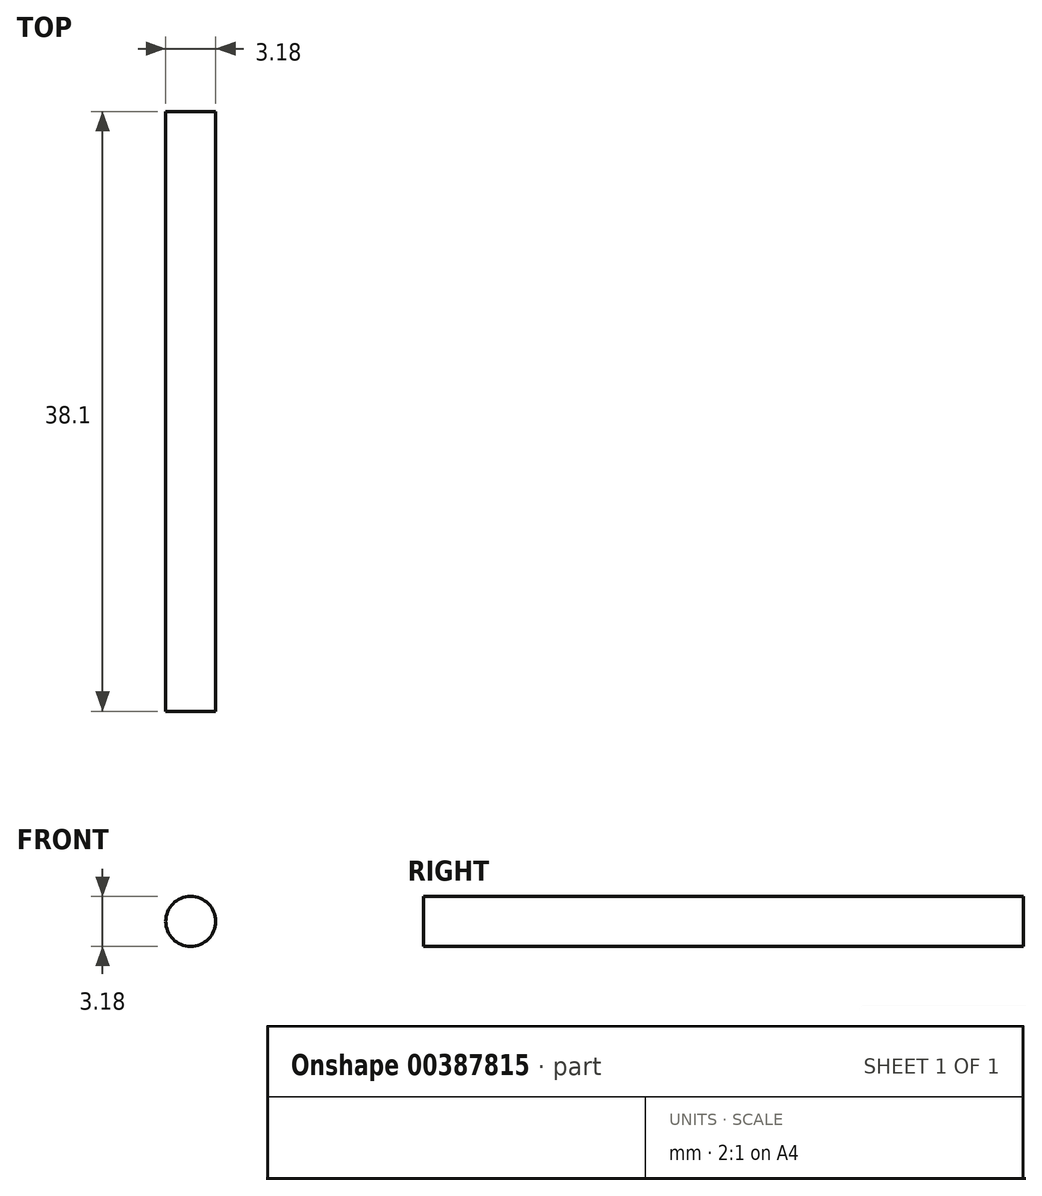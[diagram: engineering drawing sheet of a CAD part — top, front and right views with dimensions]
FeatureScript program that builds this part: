
annotation { "Feature Type Name" : "Feature", "Feature Type Description" : "" }
export const myFeature = defineFeature(function(context is Context, id is Id, definition is map)
    precondition{}
    {
        {
            var Q0;
            Q0=qCreatedBy(makeId("Front.planeOp"),FACE);
            var sketch = newSketch(context, id + "F0", { "sketchPlane" : qUnion([Q0])});
            skCircle(sketch, "E0", {"center": v(0, 0) * mm, "radius": 1.59 * mm});
            skSolve(sketch);
        }
        {
            var Q0;
            Q0 = qSketchRegion(id + "F0", true);
            extrude(context, id + "F1", {"entities" : qUnion([Q0]), "depth" : 38.1 * mm, "offsetDistance" : 25.4 * mm});
        }
    });
